# Revit family: Sanitary_Basins_Sanindusa_Look-Semi-Recessed-Washbasin
name_source: partatom
category: Plumbing Fixtures
revit_build: Autodesk Revit 2018 (Build: 20170223_1515(x64)
units: mm (PartAtom-declared; Revit-internal decimal feet)

## family parameters
Always vertical = Yes
Cut with Voids When Loaded = No
OmniClass Number = 23.45.00.00
OmniClass Title = Sanitary, Laundry, and Cleaning Equipment
Part Type = Normal
Room Calculation Point = No
Round Connector Dimension = Use Diameter
Shared = No
Work Plane-Based = Yes

## types (1)
- SanindusaLavatório134360004
    AssetType = Fixed
    Category = Pr_40_20_96_18: Counter top wash basins
    CodePerformance = EN 14688:2015 CL25
    Color = white
    Constituents = 48011-chromed embellishment ring (included), 43-fixing kit (included)
    Cost = 0 $
    Default Elevation = 1219 mm
    Description = semi-recessed basin
    DrainSize = 46 mm  [stored 0.150919 ft]
    Edition number = 1
    Features = Installation wall-mounted or placed on furniture. Glazed on all sides except on the back side, outlet zone (drain) and in the
lower setting plane of the mixer. Not rectified. Compatible with taps with and without pop up waste.
    Finish = gloss
    InstallationDate = 1900-12-31T23:59:59
    Manufacturer = Sanindusa
    ManufacturerName = Sanindusa
    ManufacturerURL = www.tec.sanindusa.pt
    Material = fine fireclay
    ModelNumber = 134360004
    ModelReference = Look
    Name = Look 83x47 semi-recessed
    NominalHeight = 177 mm
    NominalLength = 832 mm
    NominalWidth = 465 mm
    Product Guid = 6b509c7a-eb0b-4dd0-a6a4-ea4444008f92
    Product data url = https://bimobject.com
    ProductInformation = https://www.tec.sanindusa.pt
    ProductionYear = 2017
    Shape = rectangular
    Size = 83x47
    SpilloverLevel = 135 mm
    URL = www.tec.sanindusa.pt
    Uniclass2015Code = Pr_40_20_96_18
    Uniclass2015Title = Counter top wash basins
    Uniclass2015Version = Products v1.6
    Version = 2
    WarrantyDescription = https://www.tec.sanindusa.pt
    WarrantyDurationParts = 5
    WarrantyDurationUnit = year
    WarrantyStartDate = 1900-12-31T23:59:59
1900-12-31T23:59:59
    WashHandBasinMounting = other
    WashHandBasinType = other
    Weight = 18.40 kg

note: [stored X ft] marks values corroborated as IEEE doubles in the binary element streams (Revit-internal decimal feet)

## geometry (parser evidence)
native form markers: Sweep x6
no freeform markers — native parametric forms only
